FCSTD DOCUMENT  (FreeCAD 0.21R33668 +26 (Git))
Label: camera_mount_w134
License: All rights reserved
LicenseURL: http://en.wikipedia.org/wiki/All_rights_reserved
objects: Sketcher::SketchObject×1, PartDesign::Body×1
note: 2 computed .brp shape members not serialized (recipe doc carries the construction recipe); baked Part::Feature solids carry a one-line shape summary decoded from their .brp

FEATURE [Sketcher::SketchObject] Sketch
  FullyConstrained = true
  MapMode = 5
  Support = -> [XY_Plane]
  sketch-geometry (17):
    g0: LineSegment StartX=0 StartY=0 StartZ=0 EndX=134 EndY=0 EndZ=0
    g1: LineSegment StartX=0 StartY=0 StartZ=0 EndX=0 EndY=35 EndZ=0
    g2: LineSegment StartX=0 StartY=35 StartZ=0 EndX=20 EndY=35 EndZ=0
    g3: LineSegment StartX=30 StartY=45 StartZ=0 EndX=30 EndY=70 EndZ=0
    g4: LineSegment StartX=73 StartY=70 StartZ=0 EndX=73 EndY=45 EndZ=0
    g5: LineSegment StartX=83 StartY=35 StartZ=0 EndX=134 EndY=35 EndZ=0
    g6: LineSegment StartX=134 StartY=35 StartZ=0 EndX=134 EndY=0 EndZ=0
    g7: LineSegment StartX=40 StartY=80 StartZ=0 EndX=51.5 EndY=80 EndZ=0
    g8: LineSegment StartX=51.5 StartY=80 StartZ=0 EndX=63 EndY=80 EndZ=0
    g9: LineSegment StartX=20 StartY=35 StartZ=0 EndX=51.5 EndY=35 EndZ=0
    g10: LineSegment StartX=51.5 StartY=80 StartZ=0 EndX=51.5 EndY=35 EndZ=0
    g11: Circle CenterX=51.5 CenterY=58.5 CenterZ=0 NormalX=0 NormalY=0 NormalZ=1 AngleXU=0 Radius=3.175
    g12: ArcOfCircle CenterX=20 CenterY=45 CenterZ=0 NormalX=0 NormalY=0 NormalZ=1 AngleXU=0 Radius=10 StartAngle=4.71239 EndAngle=6.28319
    g13: ArcOfCircle CenterX=83 CenterY=45 CenterZ=0 NormalX=0 NormalY=0 NormalZ=1 AngleXU=0 Radius=10 StartAngle=3.14159 EndAngle=4.71239
    g14: ArcOfCircle CenterX=63 CenterY=70 CenterZ=0 NormalX=0 NormalY=0 NormalZ=1 AngleXU=0 Radius=10 StartAngle=3e-16 EndAngle=1.5708
    g15: ArcOfCircle CenterX=40 CenterY=70 CenterZ=0 NormalX=0 NormalY=0 NormalZ=1 AngleXU=0 Radius=10 StartAngle=1.5708 EndAngle=3.14159
    g16: LineSegment StartX=51.5 StartY=35 StartZ=0 EndX=83 EndY=35 EndZ=0
  constraints (44):
    c: Coincident(g0,g-1)
    c: PointOnObject(g0,g-1)
    c: DistanceX(g0,g0) = 134  'width'
    c: Coincident(g1,g0)
    c: PointOnObject(g1,g-2)
    c: DistanceY(g1,g1) = 35
    c: Coincident(g2,g1)
    c: Horizontal(g2)
    c: Vertical(g3)
    c: Vertical(g4)
    c: Horizontal(g5)
    c: Coincident(g6,g5)
    c: Coincident(g6,g0)
    c: Vertical(g6)
    c: Coincident(g7,g8)
    c: Horizontal(g7)
    c: Horizontal(g8)
    c: Horizontal(g9)
    c: Coincident(g10,g7)
    c: Coincident(g10,g9)
    c: Vertical(g10)
    c: Equal(g7,g8)
    c: DistanceX(g1,g9) = 51.5
    c: PointOnObject(g11,g10)
    c: Diameter(g11) = 6.35
    c: DistanceY(g11,g7) = 21.5
    c: Tangent(g2,g12) = -1.5708
    c: Tangent(g3,g12) = -1.5708
    c: Tangent(g4,g13) = -1.5708
    c: Tangent(g5,g13) = -1.5708
    c: Tangent(g8,g14) = 1.5708
    c: Tangent(g4,g14) = 1.5708
    c: Tangent(g7,g15) = 1.5708
    c: Tangent(g3,g15) = 1.5708
    c: DistanceY(g0,g7) = 80
    c: DistanceX(g3,g4) = 43
    c: Equal(g15,g14)
    c: Equal(g14,g13)
    c: Equal(g13,g12)
    c: Coincident(g16,g9)
    c: Coincident(g16,g5)
    c: Horizontal(g16)
    c: Coincident(g9,g2)
    c: Radius(g14) = 10
FEATURE [PartDesign::Body] Body
  Group = -> [Sketch]
  Origin = -> Origin
